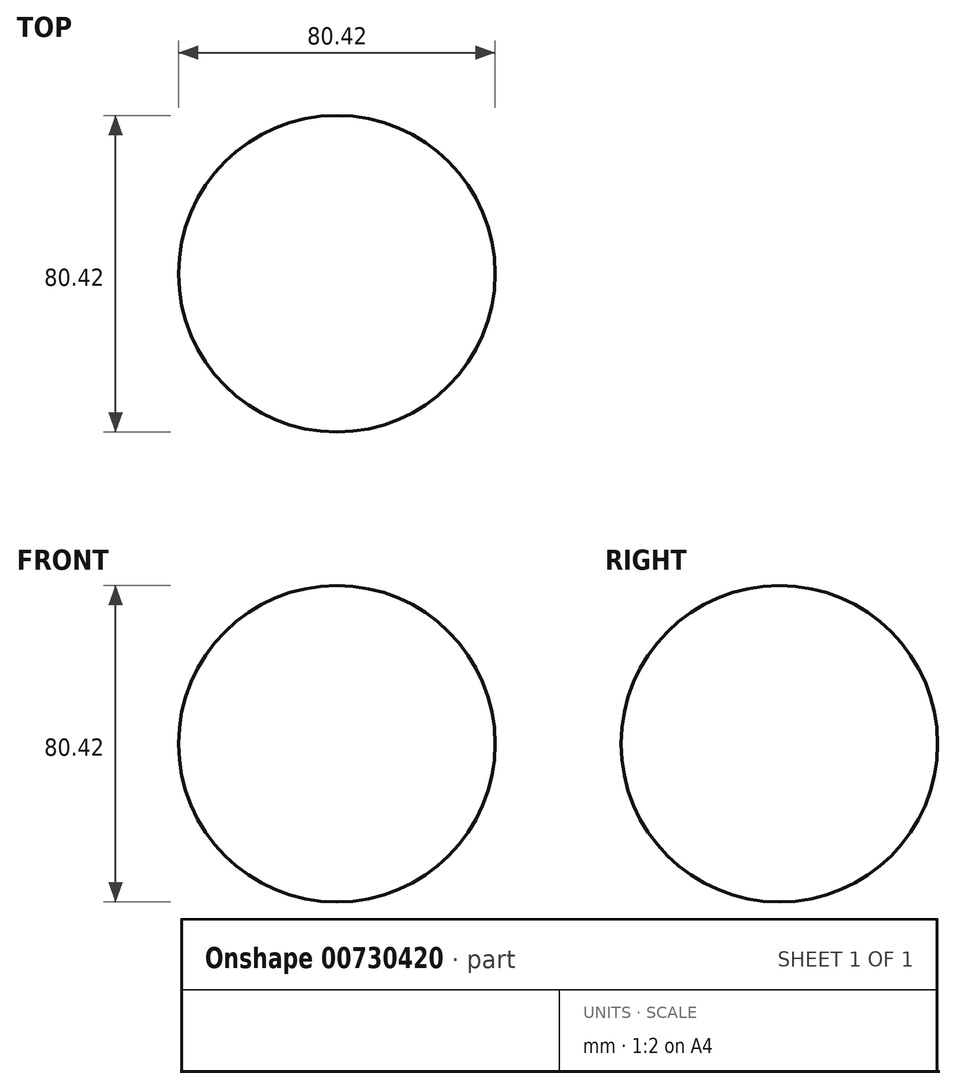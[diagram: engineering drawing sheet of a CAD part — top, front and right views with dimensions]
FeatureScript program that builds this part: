
annotation { "Feature Type Name" : "Feature", "Feature Type Description" : "" }
export const myFeature = defineFeature(function(context is Context, id is Id, definition is map)
    precondition{}
    {
        {
            var Q0;
            Q0=qCreatedBy(makeId("Front.planeOp"),FACE);
            var sketch = newSketch(context, id + "F0", { "sketchPlane" : qUnion([Q0])});
            skCircle(sketch, "E0", {"center": v(0, 0) * mm, "radius": 40.2 * mm});
            skLineSegment(sketch, "E1", {"start": v(-40.2, 0) * mm, "end": v(40.2, 0) * mm});
            skSolve(sketch);
        }
        {
            var Q0;
            {var subQ0=sQuery(id+"F0.wireOp",EDGE,"E1");Q0=makeQuery(id+"F0.imprint","IMPRINT",FACE,{"disambiguationData":[TD([[makeQuery(id+"F0.imprint","IMPRINT",EDGE,{"derivedFrom":subQ0}),-1.0]])]});}
            var Q1;
            Q1=sQuery(id+"F0.wireOp",EDGE,"E1");
            revolve(context, id + "F1", {"surfaceOperationType" : NewSurfaceOperationType.NEW, "entities" : qUnion([Q0]), "axis" : qUnion([Q1]), "revolveType" : RevolveType.FULL});
        }
    });
